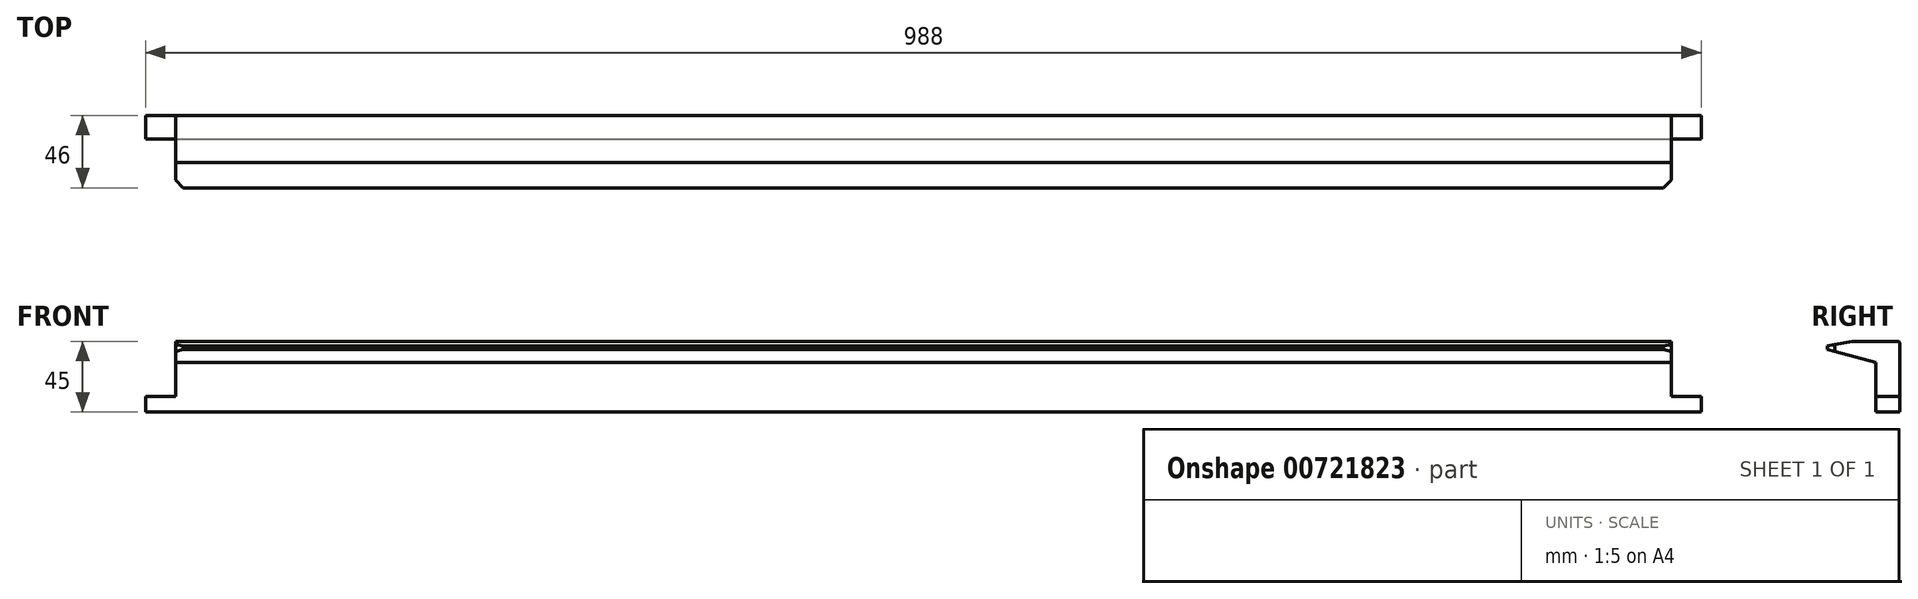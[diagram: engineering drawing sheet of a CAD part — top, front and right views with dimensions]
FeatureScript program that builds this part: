
annotation { "Feature Type Name" : "Feature", "Feature Type Description" : "" }
export const myFeature = defineFeature(function(context is Context, id is Id, definition is map)
    precondition{}
    {
        {
            var Q0;
            Q0=qCreatedBy(makeId("Right.planeOp"),FACE);
            var sketch = newSketch(context, id + "F0", { "sketchPlane" : qUnion([Q0])});
            skLineSegment(sketch, "E0", {"start": v(-1, 0) * mm, "end": v(-30, 0) * mm});
            skLineSegment(sketch, "E1", {"start": v(-30, 0) * mm, "end": v(-46, -2.82) * mm});
            skLineSegment(sketch, "E2", {"start": v(-46, -2.82) * mm, "end": v(-46, -5.18) * mm});
            skLineSegment(sketch, "E3", {"start": v(-46, -5.18) * mm, "end": v(-15, -13.5) * mm});
            skLineSegment(sketch, "E4", {"start": v(-15, -13.5) * mm, "end": v(-15, -45) * mm});
            skLineSegment(sketch, "E5", {"start": v(-15, -45) * mm, "end": v(0, -45) * mm});
            skLineSegment(sketch, "E6", {"start": v(0, -45) * mm, "end": v(0, -1) * mm});
            skPoint(sketch, "E7.visualSharp", {"position": v(0, 0) * mm});
            skArc(sketch, "E7.filletArc", {"start": v(0, -1) * mm, "mid": v(-0.3, -0.3) * mm, "end": v(-1, 0) * mm});
            skSolve(sketch);
        }
        {
            var Q0;
            Q0 = qSketchRegion(id + "F0", true);
            extrude(context, id + "F1", {"entities" : qUnion([Q0]), "oppositeDirection" : true, "depth" : 950 * mm, "offsetDistance" : 25.4 * mm});
        }
        {
            var Q0;
            Q0=qCreatedBy(makeId("Front.planeOp"),FACE);
            var sketch = newSketch(context, id + "F2", { "sketchPlane" : qUnion([Q0])});
            skLineSegment(sketch, "E8.bottom", {"start": v(19, -35) * mm, "end": v(-969, -35) * mm});
            skLineSegment(sketch, "E8.top", {"start": v(19, -45) * mm, "end": v(-969, -45) * mm});
            skLineSegment(sketch, "E8.left", {"start": v(19, -35) * mm, "end": v(19, -45) * mm});
            skLineSegment(sketch, "E8.right", {"start": v(-969, -35) * mm, "end": v(-969, -45) * mm});
            skSolve(sketch);
        }
        {
            var Q0;
            Q0 = qSketchRegion(id + "F2", true);
            extrude(context, id + "F3", {"entities" : qUnion([Q0]), "operationType" : NewBodyOperationType.ADD, "depth" : 15 * mm, "offsetDistance" : 25.4 * mm});
        }
        {
            var Q0;
            Q0=makeQuery(id+"F1.opExtrude","CAP_EDGE",EDGE,{"disambiguationData":[OSD([sQuery(id+"F0.wireOp",EDGE,"E2")])],"isStart":true});
            var Q1;
            Q1=makeQuery(id+"F1.opExtrude","CAP_EDGE",EDGE,{"disambiguationData":[OSD([sQuery(id+"F0.wireOp",EDGE,"E2")])],"isStart":false});
            chamfer(context, id + "F4", {"entities" : qUnion([Q0, Q1]), "width" : 5 * mm, "tangentPropagation" : true});
        }
    });
